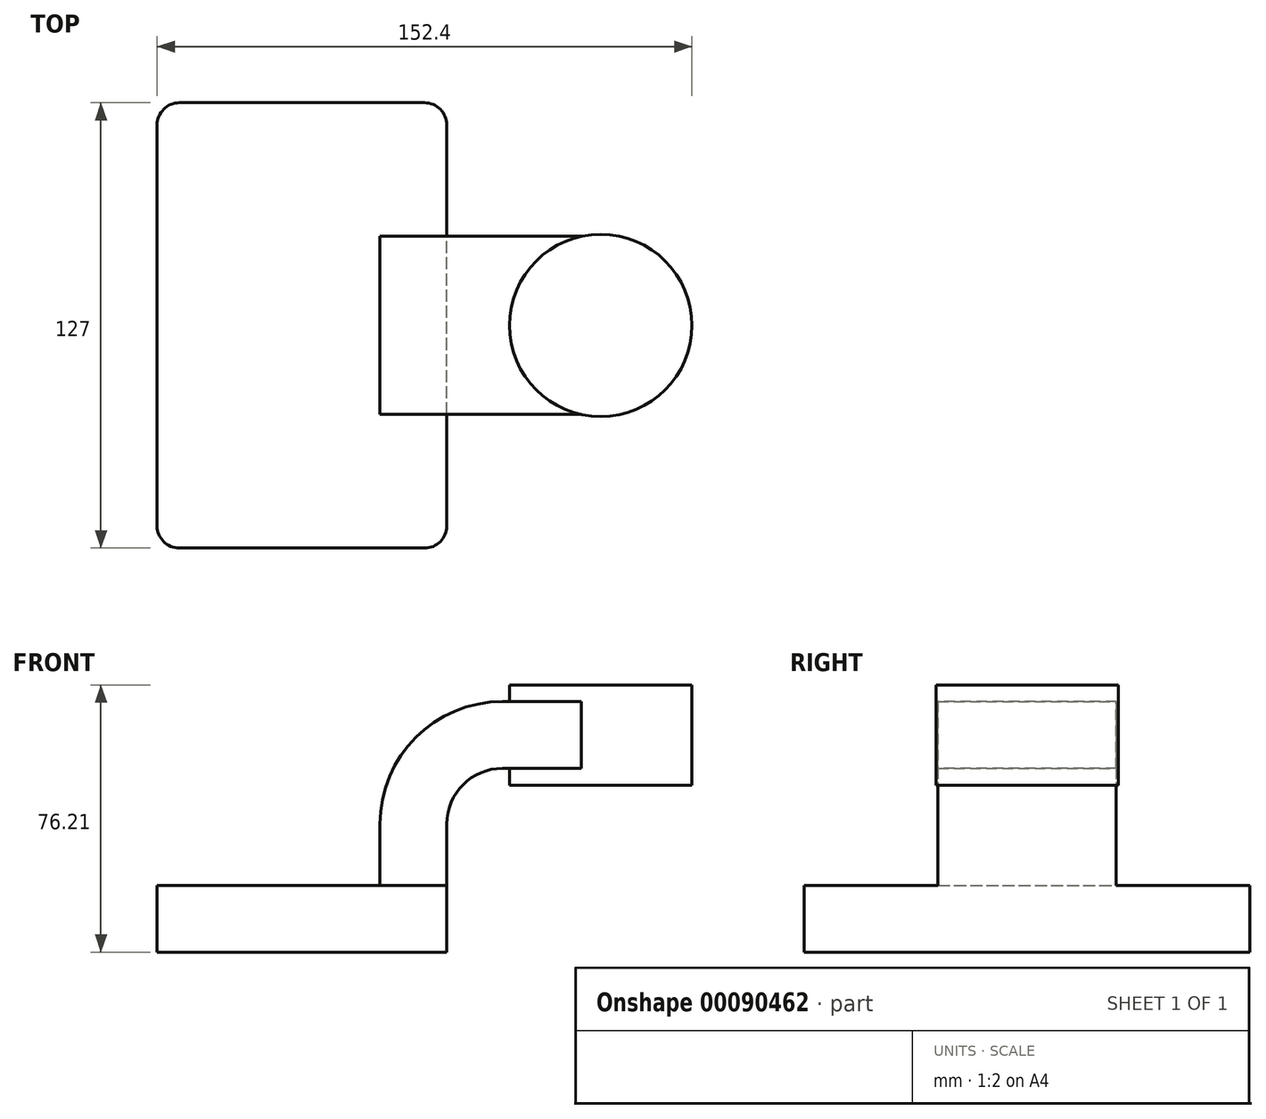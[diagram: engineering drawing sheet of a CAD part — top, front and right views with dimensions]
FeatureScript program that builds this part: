
annotation { "Feature Type Name" : "Feature", "Feature Type Description" : "" }
export const myFeature = defineFeature(function(context is Context, id is Id, definition is map)
    precondition{}
    {
        {
            var Q0;
            Q0=qCreatedBy(makeId("Front.planeOp"),FACE);
            var sketch = newSketch(context, id + "F0", { "sketchPlane" : qUnion([Q0])});
            skLineSegment(sketch, "E0.bottom", {"start": v(-41.27, -9.53) * mm, "end": v(41.28, -9.53) * mm});
            skLineSegment(sketch, "E0.top", {"start": v(-41.28, 9.53) * mm, "end": v(41.28, 9.53) * mm});
            skLineSegment(sketch, "E0.left", {"start": v(-41.28, -9.53) * mm, "end": v(-41.28, 9.53) * mm});
            skLineSegment(sketch, "E0.right", {"start": v(41.28, -9.53) * mm, "end": v(41.28, 9.52) * mm});
            skPoint(sketch, "E0.middle", {"position": v(0, 0) * mm});
            skLineSegment(sketch, "E1.bottom", {"start": v(111.12, 66.68) * mm, "end": v(60.32, 66.68) * mm});
            skLineSegment(sketch, "E1.top", {"start": v(111.12, 38.1) * mm, "end": v(60.32, 38.1) * mm});
            skLineSegment(sketch, "E1.left", {"start": v(111.12, 66.68) * mm, "end": v(111.12, 38.1) * mm});
            skLineSegment(sketch, "E1.right", {"start": v(60.32, 66.68) * mm, "end": v(60.32, 38.1) * mm});
            skPoint(sketch, "E1.middle", {"position": v(85.72, 52.39) * mm});
            skLineSegment(sketch, "E2", {"start": v(41.28, 9.52) * mm, "end": v(41.28, 27) * mm});
            skArc(sketch, "E3", {"start": v(41.27, 27) * mm, "mid": v(45.92, 38.23) * mm, "end": v(57.15, 42.88) * mm});
            skLineSegment(sketch, "E4", {"start": v(57.15, 42.88) * mm, "end": v(85.13, 42.88) * mm});
            skLineSegment(sketch, "E5.0", {"start": v(57.15, 61.93) * mm, "end": v(85.13, 61.93) * mm});
            skArc(sketch, "E5.1", {"start": v(22.22, 27) * mm, "mid": v(32.45, 51.7) * mm, "end": v(57.15, 61.93) * mm});
            skLineSegment(sketch, "E5.2", {"start": v(22.22, 9.52) * mm, "end": v(22.22, 27) * mm});
            skFitSpline(sketch, "E6", {"points": [v(-41.27, 9.53) * mm, v(57.15, 61.93) * mm], "startDerivative": vector(1.06, 63.7) * mm, "endDerivative": vector(154.43, -1.53) * mm});
            skLineSegment(sketch, "E7", {"start": v(85.13, 66.68) * mm, "end": v(85.13, 38.1) * mm});
            skSolve(sketch);
        }
        {
            var Q0;
            Q0=makeQuery(id+"F0.imprint","IMPRINT",FACE,{"disambiguationData":[TD([[makeQuery(id+"F0.imprint","IMPRINT",EDGE,{"derivedFrom":sQuery(id+"F0.wireOp",EDGE,"E0.bottom")}),1.0]])]});
            extrude(context, id + "F1", {"entities" : qUnion([Q0]), "endBound" : BoundingType.SYMMETRIC, "depth" : 127 * mm});
        }
        {
            var Q0;
            {var subQ1=sQuery(id+"F0.wireOp",EDGE,"E2");Q0=makeQuery(id+"F0.imprint","IMPRINT",FACE,{"disambiguationData":[TD([[makeQuery(id+"F0.imprint","IMPRINT",EDGE,{"derivedFrom":subQ1}),1.0]])]});}
            var Q1;
            {var subQ0=sQuery(id+"F0.wireOp",EDGE,"E5.0");var subQ1=sQuery(id+"F0.wireOp",EDGE,"E1.right");var subQ2=makeQuery(id+"F0.imprint","INTERSECT",VERTEX,{"derivedFrom":[subQ1,subQ0]});Q1=makeQuery(id+"F0.imprint","IMPRINT",FACE,{"disambiguationData":[TD([[makeQuery(id+"F0.imprint","IMPRINT",EDGE,{"disambiguationData":[TD([[subQ2,-1.0]])],"derivedFrom":subQ1}),1.0]])]});}
            extrude(context, id + "F2", {"entities" : qUnion([Q0, Q1]), "operationType" : NewBodyOperationType.ADD, "endBound" : BoundingType.SYMMETRIC, "depth" : 50.8 * mm});
        }
        {
            var Q0;
            Q0=makeQuery(id+"F0.imprint","IMPRINT",FACE,{"disambiguationData":[TD([[makeQuery(id+"F0.imprint","IMPRINT",EDGE,{"derivedFrom":sQuery(id+"F0.wireOp",EDGE,"E5.1")}),1.0]])]});
            extrude(context, id + "F3", {"entities" : qUnion([Q0]), "operationType" : NewBodyOperationType.ADD, "depth" : 15.88 * mm});
        }
        {
            var Q0;
            {var subQ0=sQuery(id+"F0.wireOp",EDGE,"E1.left");Q0=makeQuery(id+"F0.imprint","IMPRINT",FACE,{"disambiguationData":[TD([[makeQuery(id+"F0.imprint","IMPRINT",EDGE,{"derivedFrom":subQ0}),-1.0]])]});}
            var Q1;
            Q1=sQuery(id+"F0.wireOp",EDGE,"E7");
            revolve(context, id + "F4", {"operationType" : NewBodyOperationType.ADD, "entities" : qUnion([Q0]), "axis" : qUnion([Q1]), "revolveType" : RevolveType.FULL});
        }
        {
            var Q0;
            Q0=makeQuery(id+"F1.opExtrude","CAP_EDGE",EDGE,{"disambiguationData":[OSD([sQuery(id+"F0.wireOp",EDGE,"E0.right")])],"isStart":false});
            var Q1;
            Q1=makeQuery(id+"F1.opExtrude","CAP_EDGE",EDGE,{"disambiguationData":[OSD([sQuery(id+"F0.wireOp",EDGE,"E0.left")])],"isStart":false});
            var Q2;
            Q2=makeQuery(id+"F1.opExtrude","CAP_EDGE",EDGE,{"disambiguationData":[OSD([sQuery(id+"F0.wireOp",EDGE,"E0.right")])],"isStart":true});
            var Q3;
            Q3=makeQuery(id+"F1.opExtrude","CAP_EDGE",EDGE,{"disambiguationData":[OSD([sQuery(id+"F0.wireOp",EDGE,"E0.left")])],"isStart":true});
            fillet(context, id + "F5", {"entities" : qUnion([Q0, Q1, Q2, Q3]), "radius" : 6.35 * mm, "tangentPropagation" : true, "allowEdgeOverflow" : false});
        }
    });
